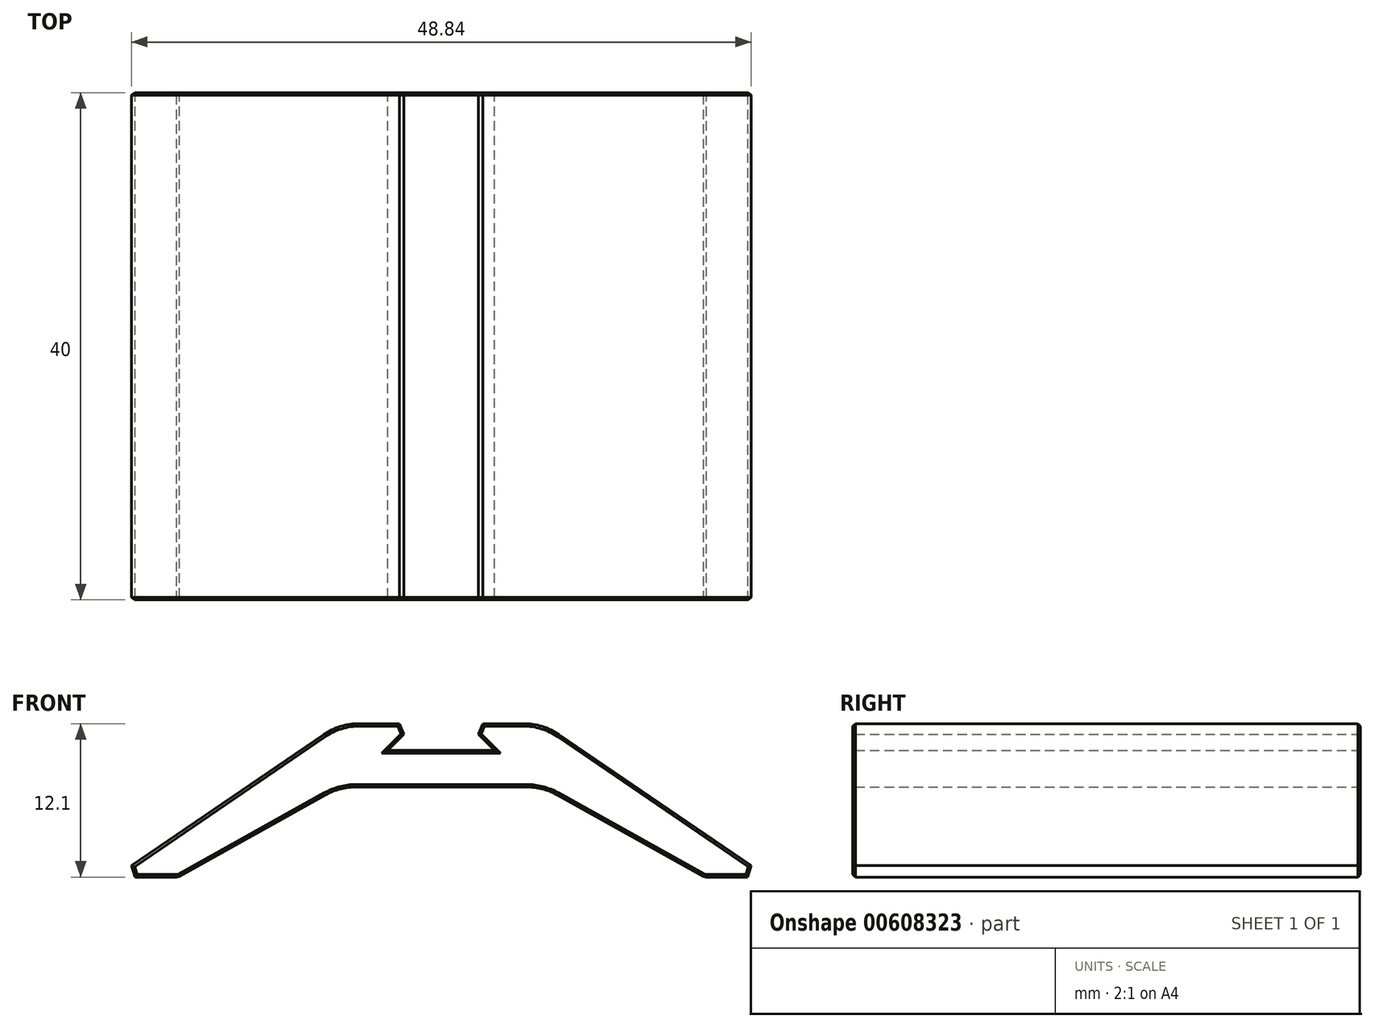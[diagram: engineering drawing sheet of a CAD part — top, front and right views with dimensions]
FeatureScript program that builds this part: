
annotation { "Feature Type Name" : "Feature", "Feature Type Description" : "" }
export const myFeature = defineFeature(function(context is Context, id is Id, definition is map)
    precondition{}
    {
        {
            var Q0;
            Q0=qCreatedBy(makeId("Front.planeOp"),FACE);
            var sketch = newSketch(context, id + "F0", { "sketchPlane" : qUnion([Q0])});
            skLineSegment(sketch, "E0", {"start": v(9.27, 2.3) * mm, "end": v(25.75, -8.94) * mm});
            skLineSegment(sketch, "E1", {"start": v(25.75, -8.94) * mm, "end": v(20.75, -8.94) * mm});
            skLineSegment(sketch, "E2", {"start": v(20.75, -8.94) * mm, "end": v(9.13, -2.47) * mm});
            skLineSegment(sketch, "E3", {"start": v(6.7, -1.84) * mm, "end": v(-6.7, -1.84) * mm});
            skLineSegment(sketch, "E4", {"start": v(-9.13, -2.47) * mm, "end": v(-20.75, -8.94) * mm});
            skLineSegment(sketch, "E5", {"start": v(-20.75, -8.94) * mm, "end": v(-25.75, -8.94) * mm});
            skLineSegment(sketch, "E6", {"start": v(-25.75, -8.94) * mm, "end": v(-9.27, 2.3) * mm});
            skLineSegment(sketch, "E7", {"start": v(-4.22, 1.04) * mm, "end": v(4.18, 1.04) * mm});
            skLineSegment(sketch, "E8", {"start": v(4.18, 1.04) * mm, "end": v(2.05, 3.16) * mm});
            skLineSegment(sketch, "E9", {"start": v(-4.22, 1.04) * mm, "end": v(-2.1, 3.16) * mm});
            skLineSegment(sketch, "E10", {"start": v(-6.46, 3.16) * mm, "end": v(-2.1, 3.16) * mm});
            skLineSegment(sketch, "E11.trimOffspring", {"start": v(2.05, 3.16) * mm, "end": v(6.46, 3.16) * mm});
            skPoint(sketch, "E12.visualSharp", {"position": v(-8, 3.16) * mm});
            skArc(sketch, "E12.filletArc", {"start": v(-6.46, 3.16) * mm, "mid": v(-7.93, 2.94) * mm, "end": v(-9.27, 2.3) * mm});
            skPoint(sketch, "E13.visualSharp", {"position": v(8, 3.16) * mm});
            skArc(sketch, "E13.filletArc", {"start": v(9.27, 2.3) * mm, "mid": v(7.93, 2.94) * mm, "end": v(6.46, 3.16) * mm});
            skPoint(sketch, "E14.visualSharp", {"position": v(-8, -1.84) * mm});
            skArc(sketch, "E14.filletArc", {"start": v(-6.7, -1.84) * mm, "mid": v(-7.96, -2) * mm, "end": v(-9.13, -2.47) * mm});
            skPoint(sketch, "E15.visualSharp", {"position": v(8, -1.84) * mm});
            skArc(sketch, "E15.filletArc", {"start": v(9.13, -2.47) * mm, "mid": v(7.96, -2) * mm, "end": v(6.7, -1.84) * mm});
            skSolve(sketch);
        }
        {
            var Q0;
            Q0=makeQuery(id+"F0.imprint","IMPRINT",FACE,{"disambiguationData":[TD([[makeQuery(id+"F0.imprint","IMPRINT",EDGE,{"derivedFrom":sQuery(id+"F0.wireOp",EDGE,"E0")}),-1.0]])]});
            extrude(context, id + "F1", {"entities" : qUnion([Q0]), "endBound" : BoundingType.SYMMETRIC, "depth" : 40 * mm, "offsetDistance" : 25 * mm});
        }
        {
            var Q0;
            Q0=makeQuery(id+"F1.opExtrude","SWEPT_EDGE",EDGE,{"disambiguationData":[OSD([sQuery(id+"F0.wireOp",EDGE,"E0"),sQuery(id+"F0.wireOp",EDGE,"E1")])]});
            var Q1;
            Q1=makeQuery(id+"F1.opExtrude","SWEPT_EDGE",EDGE,{"disambiguationData":[OSD([sQuery(id+"F0.wireOp",EDGE,"E1"),sQuery(id+"F0.wireOp",EDGE,"E2")])]});
            var Q2;
            Q2=makeQuery(id+"F1.opExtrude","SWEPT_EDGE",EDGE,{"disambiguationData":[OSD([sQuery(id+"F0.wireOp",EDGE,"E5"),sQuery(id+"F0.wireOp",EDGE,"E6")])]});
            var Q3;
            Q3=makeQuery(id+"F1.opExtrude","SWEPT_EDGE",EDGE,{"disambiguationData":[OSD([sQuery(id+"F0.wireOp",EDGE,"E4"),sQuery(id+"F0.wireOp",EDGE,"E5")])]});
            var Q4;
            Q4=makeQuery(id+"F1.opExtrude","SWEPT_EDGE",EDGE,{"disambiguationData":[OSD([sQuery(id+"F0.wireOp",EDGE,"E9"),sQuery(id+"F0.wireOp",EDGE,"E10")])]});
            var Q5;
            Q5=makeQuery(id+"F1.opExtrude","SWEPT_EDGE",EDGE,{"disambiguationData":[OSD([sQuery(id+"F0.wireOp",EDGE,"E8"),sQuery(id+"F0.wireOp",EDGE,"E11.trimOffspring")])]});
            chamfer(context, id + "F2", {"entities" : qUnion([Q0, Q1, Q2, Q3, Q4, Q5]), "width" : 0.5 * mm, "tangentPropagation" : true});
        }
        {
            var Q0;
            Q0=makeQuery(id+"F1.opExtrude","CAP_FACE",FACE,{"disambiguationData":[OSD([sQuery(id+"F0.wireOp",EDGE,"E0"),sQuery(id+"F0.wireOp",EDGE,"E1"),sQuery(id+"F0.wireOp",EDGE,"E2"),sQuery(id+"F0.wireOp",EDGE,"E3"),sQuery(id+"F0.wireOp",EDGE,"E4"),sQuery(id+"F0.wireOp",EDGE,"E5"),sQuery(id+"F0.wireOp",EDGE,"E6"),sQuery(id+"F0.wireOp",EDGE,"E7"),sQuery(id+"F0.wireOp",EDGE,"E8"),sQuery(id+"F0.wireOp",EDGE,"E9"),sQuery(id+"F0.wireOp",EDGE,"E10"),sQuery(id+"F0.wireOp",EDGE,"E11.trimOffspring"),sQuery(id+"F0.wireOp",EDGE,"E12.filletArc"),sQuery(id+"F0.wireOp",EDGE,"E13.filletArc"),sQuery(id+"F0.wireOp",EDGE,"E14.filletArc"),sQuery(id+"F0.wireOp",EDGE,"E15.filletArc")])],"isStart":true});
            var Q1;
            Q1=makeQuery(id+"F1.opExtrude","CAP_FACE",FACE,{"disambiguationData":[OSD([sQuery(id+"F0.wireOp",EDGE,"E0"),sQuery(id+"F0.wireOp",EDGE,"E1"),sQuery(id+"F0.wireOp",EDGE,"E2"),sQuery(id+"F0.wireOp",EDGE,"E3"),sQuery(id+"F0.wireOp",EDGE,"E4"),sQuery(id+"F0.wireOp",EDGE,"E5"),sQuery(id+"F0.wireOp",EDGE,"E6"),sQuery(id+"F0.wireOp",EDGE,"E7"),sQuery(id+"F0.wireOp",EDGE,"E8"),sQuery(id+"F0.wireOp",EDGE,"E9"),sQuery(id+"F0.wireOp",EDGE,"E10"),sQuery(id+"F0.wireOp",EDGE,"E11.trimOffspring"),sQuery(id+"F0.wireOp",EDGE,"E12.filletArc"),sQuery(id+"F0.wireOp",EDGE,"E13.filletArc"),sQuery(id+"F0.wireOp",EDGE,"E14.filletArc"),sQuery(id+"F0.wireOp",EDGE,"E15.filletArc")])],"isStart":false});
            chamfer(context, id + "F3", {"entities" : qUnion([Q0, Q1]), "width" : 0.2 * mm, "tangentPropagation" : true});
        }
    });
